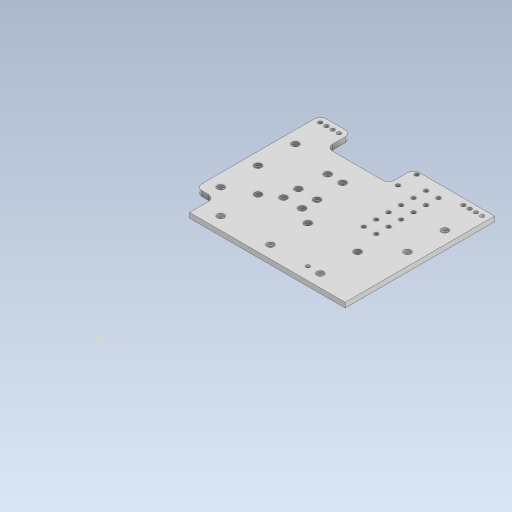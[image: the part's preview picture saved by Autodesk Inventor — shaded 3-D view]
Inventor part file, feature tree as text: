
AUTODESK INVENTOR PART (.ipt)
format: ipt  version: 2023.5 (Build 275446000, 446)  size: 522,240 bytes
history: native  units: in
note: dims shown in document units (in); Inventor stores cm internally (conversion verified against a paired STEP export)
features: sketch x2, extrude x2, fillet x1
ambient origin geometry x8: Origin, YZ Plane, XZ Plane, XY Plane, X Axis, Y Axis, Z Axis, Center Point
bodies: Solid1 (feature_tree)
feature tree (5):
  sketch  "Sketch1"  dims[d29=0.1575in d30=0.0in d31=0.0787in d32=0.0in]
  extrude  "Extrusion1"  Depth=0.0787in TaperAngle=0.0deg
  sketch  "Sketch2"  dims[d33=5.5118in d34=4.7244in d35=0.3937in d36=0.3937in d37=0.3937in d39=0.3937in d40=0.3937in d41=0.3937in d42=0.3937in d43=0.3937in d44=1.5748in d45=1.5748in d46=0.126in d47=0.0984in d48=0.1969in d49=0.126in d50=0.5906in d60=0.126in d61=0.126in d63=0.126in d65=0.126in d66=0.3937in d69=0.3937in d70=0.3937in d71=0.3937in d76=0.1299in d77=0.2165in d78=1.1811in d79=0.1299in d80=0.2165in d81=0.5906in d82=0.7874in d83=0.1969in d84=0.126in d85=0.3937in]
  extrude  "Extrusion2"  Depth=4.7244in
  fillet  "Fillet1"  Radius=0.3937in
